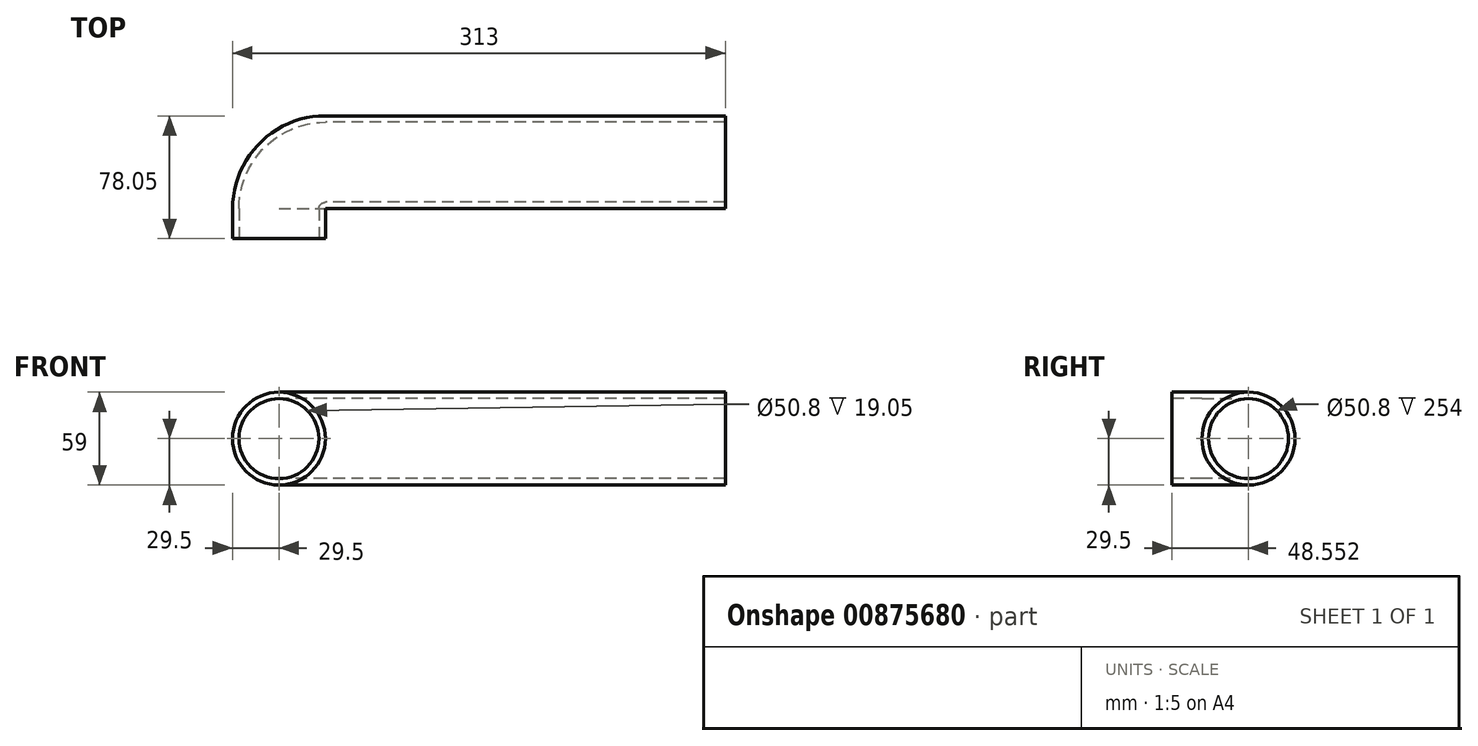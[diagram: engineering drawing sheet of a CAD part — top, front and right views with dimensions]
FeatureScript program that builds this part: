
annotation { "Feature Type Name" : "Feature", "Feature Type Description" : "" }
export const myFeature = defineFeature(function(context is Context, id is Id, definition is map)
    precondition{}
    {
        {
            var Q0;
            Q0=qCreatedBy(makeId("Front.planeOp"),FACE);
            var sketch = newSketch(context, id + "F0", { "sketchPlane" : qUnion([Q0])});
            skCircle(sketch, "E0", {"center": v(0, 0) * mm, "radius": 25.4 * mm});
            skCircle(sketch, "E1", {"center": v(0, 0) * mm, "radius": 29.5 * mm});
            skSolve(sketch);
        }
        {
            var Q0;
            Q0=qCreatedBy(makeId("Top.planeOp"),FACE);
            var sketch = newSketch(context, id + "F1", { "sketchPlane" : qUnion([Q0])});
            skArc(sketch, "E2", {"start": v(0, 0) * mm, "mid": v(8.64, 20.86) * mm, "end": v(29.5, 29.5) * mm});
            skLineSegment(sketch, "E3", {"start": v(0, 0) * mm, "end": v(0, -19.05) * mm});
            skLineSegment(sketch, "E4", {"start": v(29.5, 29.5) * mm, "end": v(283.5, 29.5) * mm});
            skSolve(sketch);
        }
        {
            var Q0;
            Q0 = qSketchRegion(id + "F0", true);
            var Q1;
            Q1 = qConstructionFilter(qBodyType(qCreatedBy(id + "F1" ,EDGE), BodyType.WIRE), ConstructionObject.NO);
            sweep(context, id + "F2", {"profiles" : qUnion([Q0]), "path" : qUnion([Q1])});
        }
    });
